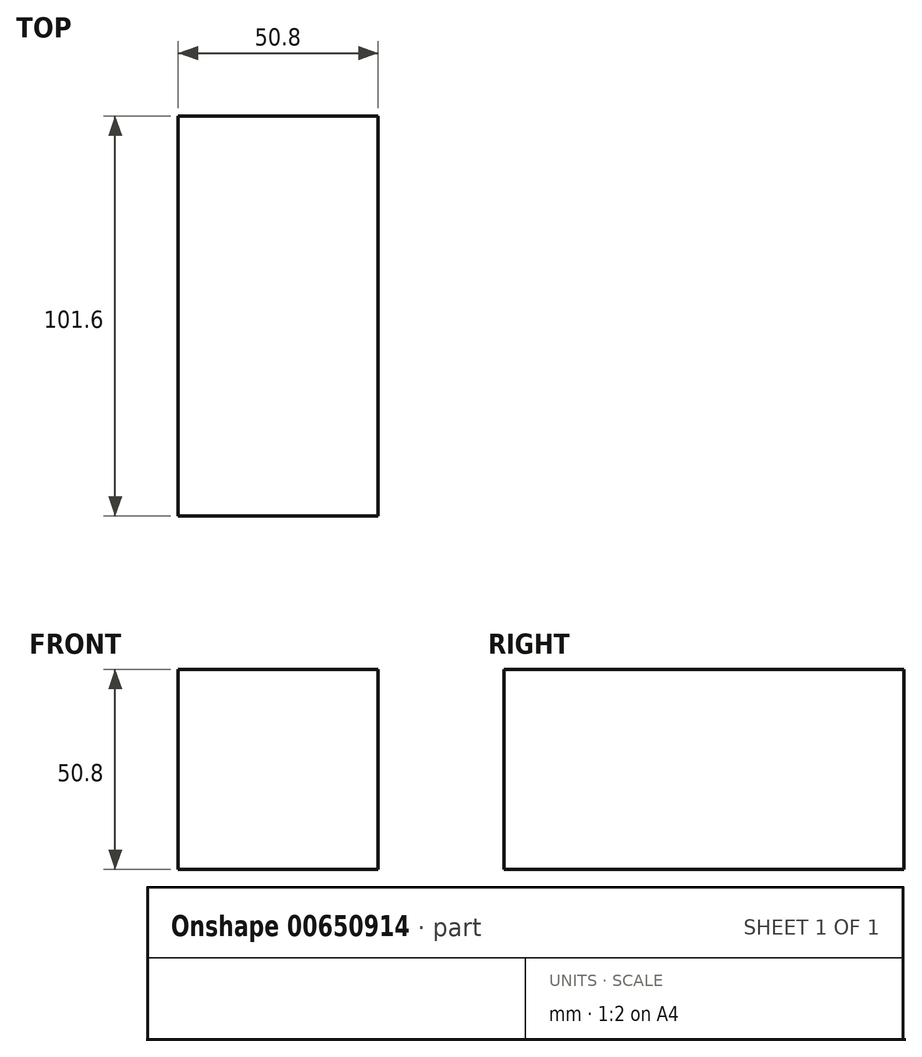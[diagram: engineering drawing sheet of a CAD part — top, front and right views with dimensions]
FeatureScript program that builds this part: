
annotation { "Feature Type Name" : "Feature", "Feature Type Description" : "" }
export const myFeature = defineFeature(function(context is Context, id is Id, definition is map)
    precondition{}
    {
        {
            var Q0;
            Q0=qCreatedBy(makeId("Top.planeOp"),FACE);
            var sketch = newSketch(context, id + "F0", { "sketchPlane" : qUnion([Q0])});
            skLineSegment(sketch, "E0.bottom", {"start": v(-25.4, 50.8) * mm, "end": v(25.4, 50.8) * mm});
            skLineSegment(sketch, "E0.top", {"start": v(-25.4, -50.8) * mm, "end": v(25.4, -50.8) * mm});
            skLineSegment(sketch, "E0.left", {"start": v(-25.4, 50.8) * mm, "end": v(-25.4, -50.8) * mm});
            skLineSegment(sketch, "E0.right", {"start": v(25.4, 50.8) * mm, "end": v(25.4, -50.8) * mm});
            skPoint(sketch, "E0.middle", {"position": v(0, 0) * mm});
            skPoint(sketch, "E1", {"position": v(0, -50.8) * mm});
            skPoint(sketch, "E2", {"position": v(-12.7, -50.8) * mm});
            skPoint(sketch, "E3", {"position": v(12.7, -50.8) * mm});
            skLineSegment(sketch, "E4.bottom", {"start": v(-12.7, -50.8) * mm, "end": v(12.7, -50.8) * mm});
            skLineSegment(sketch, "E4.top", {"start": v(-12.7, -101.6) * mm, "end": v(12.7, -101.6) * mm});
            skLineSegment(sketch, "E4.left", {"start": v(-12.7, -50.8) * mm, "end": v(-12.7, -101.6) * mm});
            skLineSegment(sketch, "E4.right", {"start": v(12.7, -50.8) * mm, "end": v(12.7, -101.6) * mm});
            skSolve(sketch);
        }
        {
            var Q0;
            Q0=makeQuery(id+"F0.imprint","IMPRINT",FACE,{"disambiguationData":[TD([[makeQuery(id+"F0.imprint","IMPRINT",EDGE,{"derivedFrom":sQuery(id+"F0.wireOp",EDGE,"E0.bottom")}),-1.0]])]});
            var Q1;
            Q1=makeQuery(id+"F0.imprint","IMPRINT",FACE,{"disambiguationData":[TD([[makeQuery(id+"F0.imprint","IMPRINT",EDGE,{"derivedFrom":sQuery(id+"F0.wireOp",EDGE,"E4.bottom")}),-1.0]])]});
            extrude(context, id + "F1", {"entities" : qUnion([Q0, Q1]), "depth" : 50.8 * mm, "offsetDistance" : 25.4 * mm});
        }
    });
